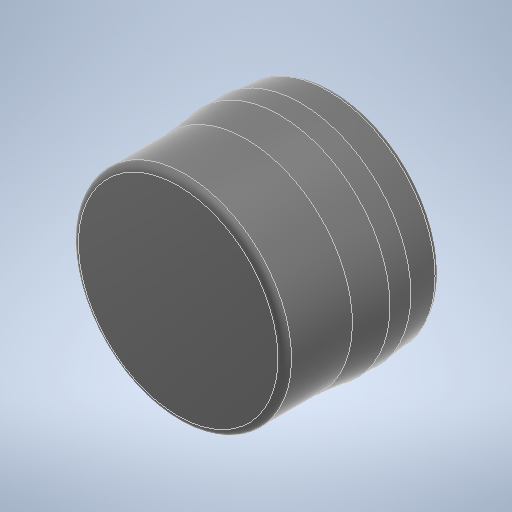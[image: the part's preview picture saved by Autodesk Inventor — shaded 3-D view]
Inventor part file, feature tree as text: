
AUTODESK INVENTOR PART (.ipt)
format: ipt  version: 2025.1 (Build 291241020, 241B)  size: 637,952 bytes
history: native  units: mm
features: revolve x2, sketch x2, fillet x1, projected_geometry x1
ambient origin geometry x8: Origin, YZ Plane, XZ Plane, XY Plane, X Axis, Y Axis, Z Axis, Center Point
bodies: Solid1 (feature_tree)
feature tree (6):
  revolve  "Revolution1"  [1 undecoded]
  revolve  "Revolution2"  [1 undecoded]
  fillet  "Fillet2"  [1 undecoded]
  sketch  "Sketch1"  dims[d0=15.75mm d1=10.2mm]
  sketch  "Sketch3"  dims[d2=10.0mm d3=5.0mm d4=360.0deg d14=0.8mm d15=16.3mm d16=5.0mm d17=90.0deg d19=0.8mm d20=1.0mm d21=3.0mm d22=5.0mm d25=0.8mm]
  projected_geometry  "Projected Loop1"
note: 3 required parameter values undecoded (feature->parameter linkage not recoverable at this tier; creation-order binding heuristic only, values carry confidence <= 0.55)